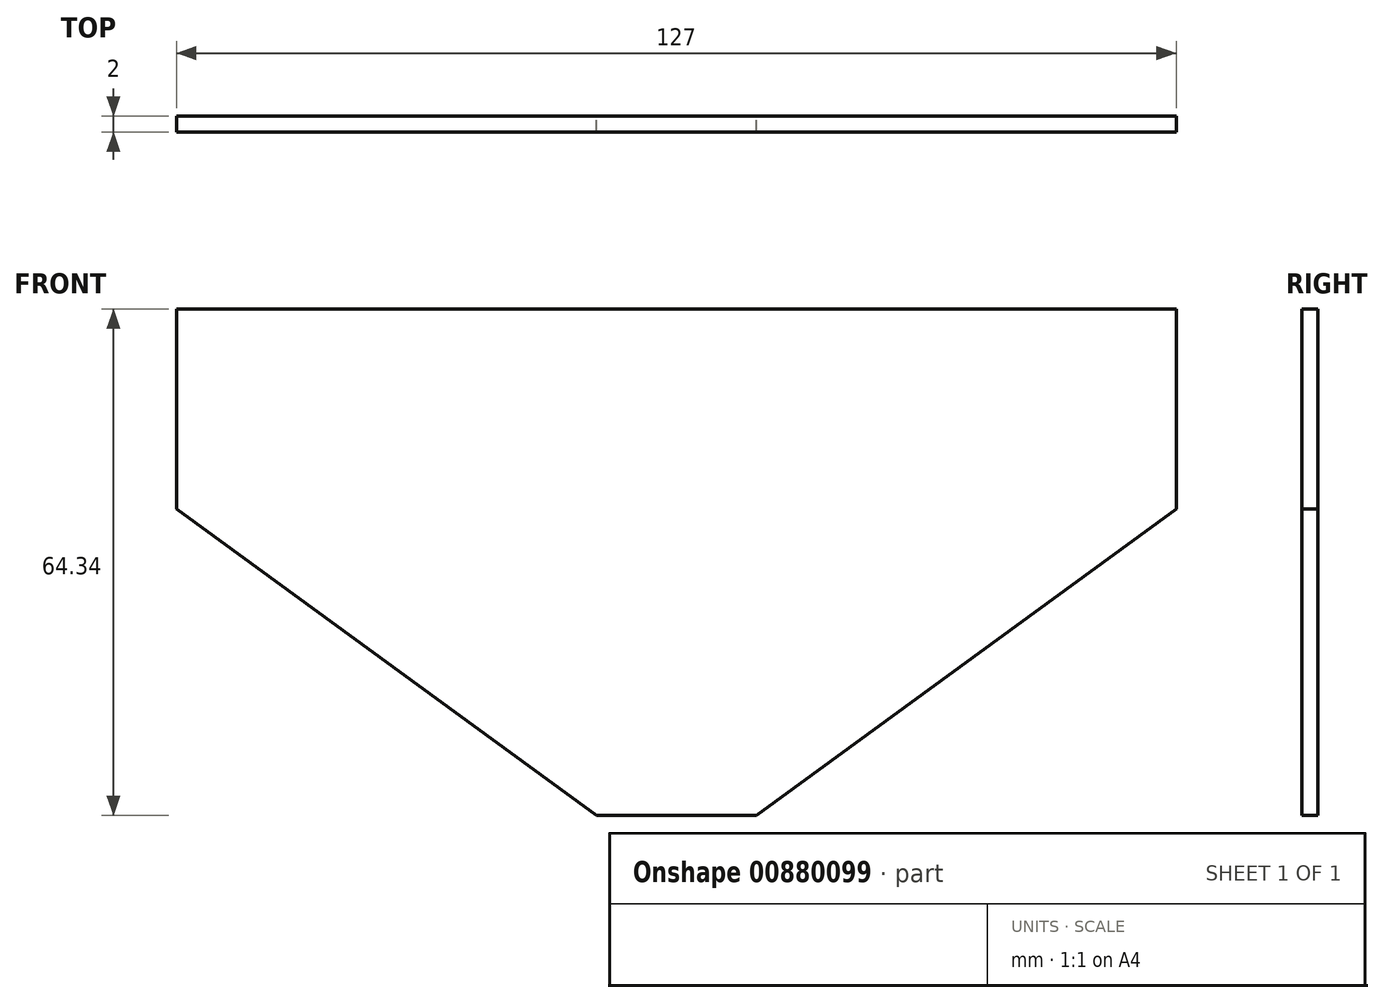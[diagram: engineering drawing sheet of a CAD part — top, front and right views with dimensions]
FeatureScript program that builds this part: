
annotation { "Feature Type Name" : "Feature", "Feature Type Description" : "" }
export const myFeature = defineFeature(function(context is Context, id is Id, definition is map)
    precondition{}
    {
        {
            var Q0;
            Q0=qCreatedBy(makeId("Front.planeOp"),FACE);
            var sketch = newSketch(context, id + "F0", { "sketchPlane" : qUnion([Q0])});
            skLineSegment(sketch, "E0.bottom", {"start": v(-63.12, 25.4) * mm, "end": v(63.88, 25.4) * mm});
            skLineSegment(sketch, "E0.top", {"start": v(-9.78, -38.94) * mm, "end": v(10.54, -38.94) * mm});
            skLineSegment(sketch, "E0.left", {"start": v(-63.12, 25.4) * mm, "end": v(-63.12, 0) * mm});
            skLineSegment(sketch, "E0.right", {"start": v(63.88, 25.4) * mm, "end": v(63.88, 0) * mm});
            skLineSegment(sketch, "E1", {"start": v(-63.12, 0) * mm, "end": v(-9.78, -38.94) * mm});
            skPoint(sketch, "E1.startSnap0", {"position": v(-63.12, 0) * mm});
            skLineSegment(sketch, "E2", {"start": v(63.88, 0) * mm, "end": v(10.54, -38.94) * mm});
            skSolve(sketch);
        }
        {
            var Q0;
            Q0 = qSketchRegion(id + "F0", true);
            extrude(context, id + "F1", {"entities" : qUnion([Q0]), "depth" : 2 * mm, "offsetDistance" : 25.4 * mm});
        }
    });
